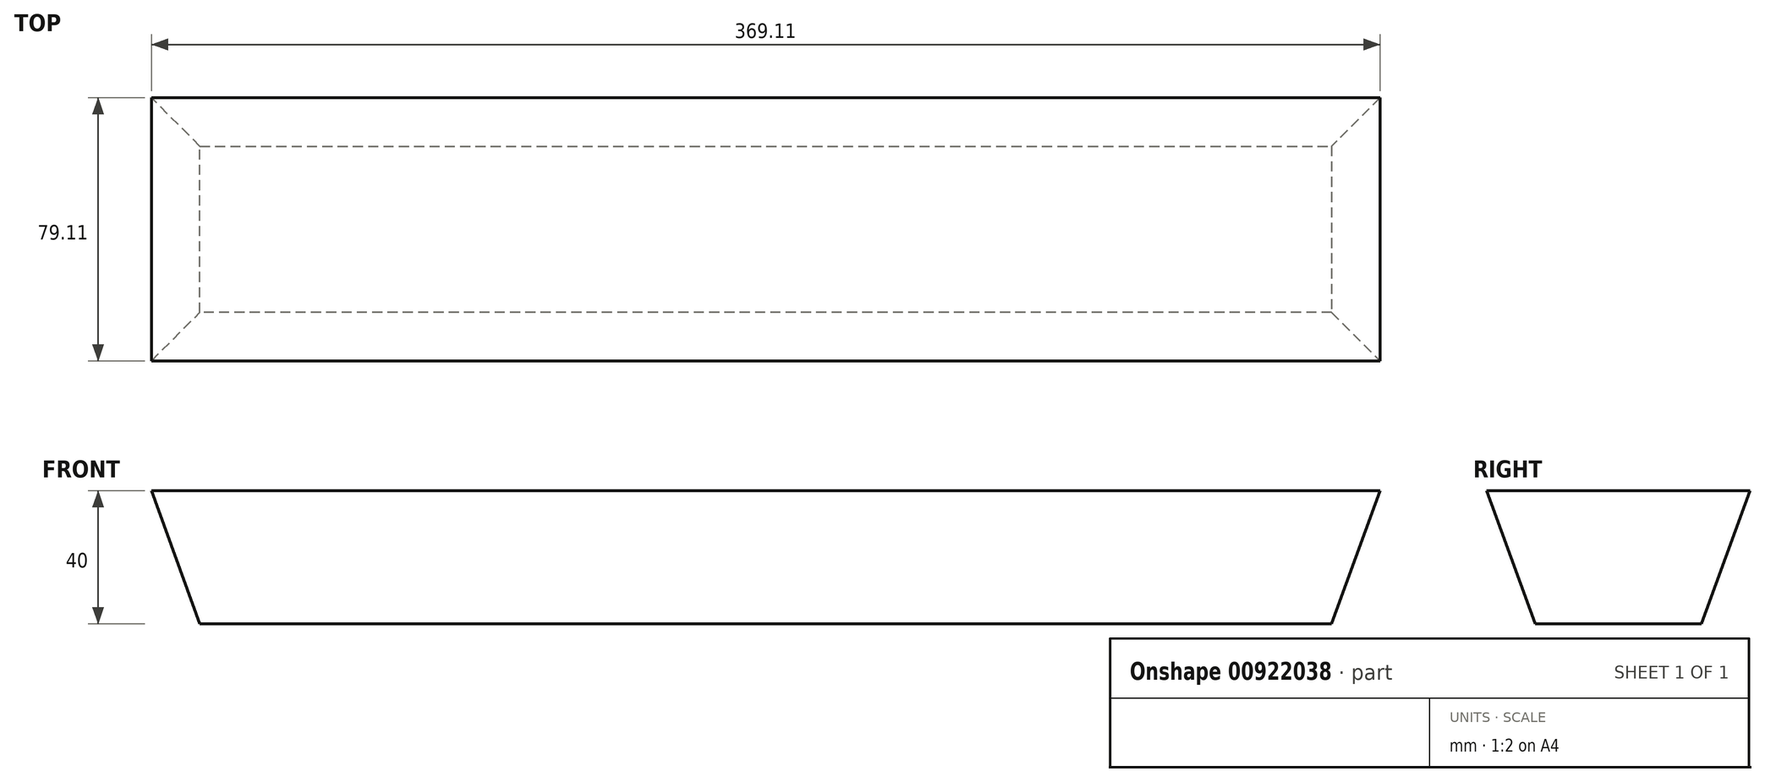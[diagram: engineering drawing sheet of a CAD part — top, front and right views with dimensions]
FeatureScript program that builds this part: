
annotation { "Feature Type Name" : "Feature", "Feature Type Description" : "" }
export const myFeature = defineFeature(function(context is Context, id is Id, definition is map)
    precondition{}
    {
        {
            var Q0;
            Q0=qCreatedBy(makeId("Top.planeOp"),FACE);
            var sketch = newSketch(context, id + "F0", { "sketchPlane" : qUnion([Q0])});
            skLineSegment(sketch, "E0.bottom", {"start": v(-165.8, -19.58) * mm, "end": v(174.2, -19.58) * mm});
            skLineSegment(sketch, "E0.top", {"start": v(-165.8, -69.58) * mm, "end": v(174.2, -69.58) * mm});
            skLineSegment(sketch, "E0.left", {"start": v(-165.8, -19.58) * mm, "end": v(-165.8, -69.58) * mm});
            skLineSegment(sketch, "E0.right", {"start": v(174.2, -19.58) * mm, "end": v(174.2, -69.58) * mm});
            skSolve(sketch);
        }
        {
            var Q0;
            Q0=makeQuery(id+"F0.imprint","IMPRINT",FACE,{"disambiguationData":[TD([[makeQuery(id+"F0.imprint","IMPRINT",EDGE,{"derivedFrom":sQuery(id+"F0.wireOp",EDGE,"E0.bottom")}),-1.0]])]});
            var sketch = newSketch(context, id + "F1", { "sketchPlane" : qUnion([Q0])});
            skSolve(sketch);
        }
        {
            var Q0;
            Q0=makeQuery(id+"F1.imprint","IMPRINT",FACE,{"disambiguationData":[TD([[makeQuery(id+"F1.imprint","IMPRINT",EDGE,{"derivedFrom":makeQuery(id+"F0.imprint","IMPRINT",EDGE,{"derivedFrom":sQuery(id+"F0.wireOp",EDGE,"E0.bottom")})}),-1.0]])]});
            extrude(context, id + "F2", {"entities" : qUnion([Q0]), "depth" : 40 * mm, "offsetDistance" : 25 * mm, "hasDraft" : true, "draftAngle" : 20 * degree});
        }
    });
